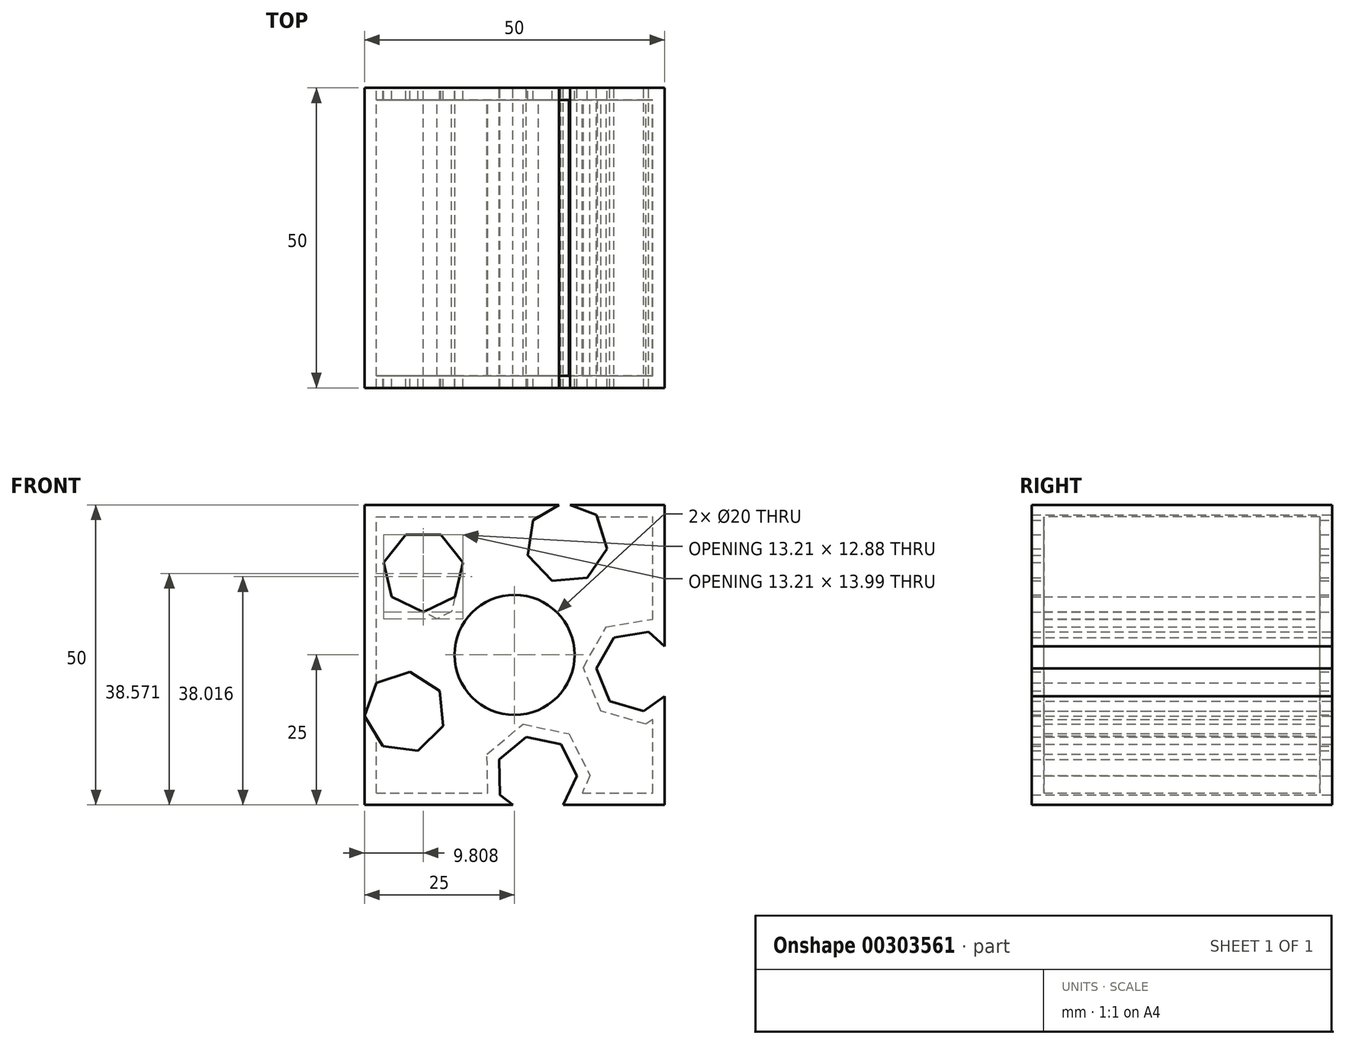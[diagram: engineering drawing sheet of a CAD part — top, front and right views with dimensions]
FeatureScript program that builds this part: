
annotation { "Feature Type Name" : "Feature", "Feature Type Description" : "" }
export const myFeature = defineFeature(function(context is Context, id is Id, definition is map)
    precondition{}
    {
        {
            var Q0;
            Q0=qCreatedBy(makeId("Front.planeOp"),FACE);
            var sketch = newSketch(context, id + "F0", { "sketchPlane" : qUnion([Q0])});
            skLineSegment(sketch, "E0.bottom", {"start": v(0, 0) * mm, "end": v(50, 0) * mm});
            skLineSegment(sketch, "E0.top", {"start": v(0, 50) * mm, "end": v(50, 50) * mm});
            skLineSegment(sketch, "E0.left", {"start": v(0, 0) * mm, "end": v(0, 50) * mm});
            skLineSegment(sketch, "E0.right", {"start": v(50, 0) * mm, "end": v(50, 50) * mm});
            skCircle(sketch, "E1", {"center": v(25, 25) * mm, "radius": 10 * mm});
            skPoint(sketch, "E1.centerSnap0", {"position": v(25, 50) * mm});
            skPoint(sketch, "E1.centerSnap1", {"position": v(50, 25) * mm});
            skLineSegment(sketch, "E2.0", {"start": v(6.87, 45.01) * mm, "end": v(12.75, 45.01) * mm});
            skLineSegment(sketch, "E2.1", {"start": v(12.75, 45.01) * mm, "end": v(16.41, 40.41) * mm});
            skLineSegment(sketch, "E2.2", {"start": v(16.41, 40.41) * mm, "end": v(15.1, 34.68) * mm});
            skLineSegment(sketch, "E2.3", {"start": v(15.1, 34.68) * mm, "end": v(9.8, 32.13) * mm});
            skLineSegment(sketch, "E2.4", {"start": v(9.8, 32.13) * mm, "end": v(4.51, 34.68) * mm});
            skLineSegment(sketch, "E2.5", {"start": v(4.51, 34.68) * mm, "end": v(3.2, 40.41) * mm});
            skLineSegment(sketch, "E2.6", {"start": v(3.2, 40.41) * mm, "end": v(6.87, 45.01) * mm});
            skPoint(sketch, "E2.0.midPoint", {"position": v(9.8, 45.01) * mm});
            skPoint(sketch, "E2.cCircle.center.orphan", {"position": v(9.8, 38.9) * mm});
            skLineSegment(sketch, "E3", {"start": v(0, 50) * mm, "end": v(50, 0) * mm, "construction": true});
            skPoint(sketch, "E4.1.1", {"position": v(48.84, 32.52) * mm});
            skPoint(sketch, "E4.1.2", {"position": v(33.7, 43.67) * mm});
            skPoint(sketch, "E4.1.3", {"position": v(39.52, 45.5) * mm});
            skLineSegment(sketch, "E4.1.4", {"start": v(40.4, 42.7) * mm, "end": v(37.12, 37.82) * mm});
            skLineSegment(sketch, "E4.1.5", {"start": v(38.63, 48.31) * mm, "end": v(40.4, 42.7) * mm});
            skLineSegment(sketch, "E4.1.6", {"start": v(37.12, 37.82) * mm, "end": v(31.26, 37.35) * mm});
            skLineSegment(sketch, "E4.1.7", {"start": v(31.26, 37.35) * mm, "end": v(27.23, 41.63) * mm});
            skLineSegment(sketch, "E4.1.8", {"start": v(27.23, 41.63) * mm, "end": v(28.07, 47.45) * mm});
            skLineSegment(sketch, "E4.1.9", {"start": v(28.07, 47.45) * mm, "end": v(33.15, 50.42) * mm});
            skLineSegment(sketch, "E4.1.10", {"start": v(33.15, 50.42) * mm, "end": v(38.63, 48.31) * mm});
            skPoint(sketch, "E4.2.1", {"position": v(39.34, 4.52) * mm});
            skPoint(sketch, "E4.2.2", {"position": v(45.42, 22.32) * mm});
            skPoint(sketch, "E4.2.3", {"position": v(48.92, 17.32) * mm});
            skLineSegment(sketch, "E4.2.4", {"start": v(46.51, 15.64) * mm, "end": v(40.88, 17.3) * mm});
            skLineSegment(sketch, "E4.2.5", {"start": v(51.33, 19) * mm, "end": v(46.51, 15.64) * mm});
            skLineSegment(sketch, "E4.2.6", {"start": v(40.88, 17.3) * mm, "end": v(38.66, 22.74) * mm});
            skLineSegment(sketch, "E4.2.7", {"start": v(38.66, 22.74) * mm, "end": v(41.54, 27.87) * mm});
            skLineSegment(sketch, "E4.2.8", {"start": v(41.54, 27.87) * mm, "end": v(47.34, 28.82) * mm});
            skLineSegment(sketch, "E4.2.9", {"start": v(47.34, 28.82) * mm, "end": v(51.7, 24.88) * mm});
            skLineSegment(sketch, "E4.2.10", {"start": v(51.7, 24.88) * mm, "end": v(51.33, 19) * mm});
            skPoint(sketch, "E4.3.1", {"position": v(9.78, 5.17) * mm});
            skPoint(sketch, "E4.3.2", {"position": v(28.59, 4.72) * mm});
            skPoint(sketch, "E4.3.3", {"position": v(24.87, -0.12) * mm});
            skLineSegment(sketch, "E4.3.4", {"start": v(22.54, 1.67) * mm, "end": v(22.43, 7.54) * mm});
            skLineSegment(sketch, "E4.3.5", {"start": v(27.2, -1.91) * mm, "end": v(22.54, 1.67) * mm});
            skLineSegment(sketch, "E4.3.6", {"start": v(22.43, 7.54) * mm, "end": v(26.96, 11.3) * mm});
            skLineSegment(sketch, "E4.3.7", {"start": v(26.96, 11.3) * mm, "end": v(32.71, 10.1) * mm});
            skLineSegment(sketch, "E4.3.8", {"start": v(32.71, 10.1) * mm, "end": v(35.36, 4.85) * mm});
            skLineSegment(sketch, "E4.3.9", {"start": v(35.36, 4.85) * mm, "end": v(32.9, -0.5) * mm});
            skLineSegment(sketch, "E4.3.10", {"start": v(32.9, -0.5) * mm, "end": v(27.2, -1.91) * mm});
            skPoint(sketch, "E4.4.1", {"position": v(1.5, 33.55) * mm});
            skPoint(sketch, "E4.4.2", {"position": v(6.74, 15.48) * mm});
            skPoint(sketch, "E4.4.3", {"position": v(1, 17.57) * mm});
            skLineSegment(sketch, "E4.4.4", {"start": v(2, 20.33) * mm, "end": v(7.58, 22.2) * mm});
            skLineSegment(sketch, "E4.4.5", {"start": v(0, 14.8) * mm, "end": v(2, 20.33) * mm});
            skLineSegment(sketch, "E4.4.6", {"start": v(7.58, 22.2) * mm, "end": v(12.52, 19.01) * mm});
            skLineSegment(sketch, "E4.4.7", {"start": v(12.52, 19.01) * mm, "end": v(13.1, 13.16) * mm});
            skLineSegment(sketch, "E4.4.8", {"start": v(13.1, 13.16) * mm, "end": v(8.9, 9.06) * mm});
            skLineSegment(sketch, "E4.4.9", {"start": v(8.9, 9.06) * mm, "end": v(3.06, 9.79) * mm});
            skLineSegment(sketch, "E4.4.10", {"start": v(3.06, 9.79) * mm, "end": v(0, 14.8) * mm});
            skLineSegment(sketch, "E4.anchor1", {"start": v(25, 25) * mm, "end": v(4.51, 34.68) * mm, "construction": true});
            skLineSegment(sketch, "E4.anchor2", {"start": v(25, 25) * mm, "end": v(8.9, 9.06) * mm, "construction": true});
            skSolve(sketch);
        }
        {
            assignVariable(context, id + "F1", {"name" : "extrusion", "anyValue" : 50});
        }
        {
            var Q0;
            Q0=makeQuery(id+"F0.imprint","IMPRINT",FACE,{"disambiguationData":[TD([[makeQuery(id+"F0.imprint","IMPRINT",EDGE,{"derivedFrom":sQuery(id+"F0.wireOp",EDGE,"E2.0")}),1.0]])]});
            extrude(context, id + "F2", {"entities" : qUnion([Q0]), "depth" : (getVariable(context, 'extrusion')) * mm});
        }
        {
            var Q0;
            Q0=makeQuery(id+"F2.opExtrude","SWEPT_FACE",FACE,{"disambiguationData":[OSD([sQuery(id+"F0.wireOp",EDGE,"E1")])]});
            var Q1;
            Q1=makeQuery(id+"F2.opExtrude","SWEPT_FACE",FACE,{"disambiguationData":[OSD([sQuery(id+"F0.wireOp",EDGE,"E4.4.10")])]});
            var Q2;
            Q2=makeQuery(id+"F2.opExtrude","SWEPT_FACE",FACE,{"disambiguationData":[OSD([sQuery(id+"F0.wireOp",EDGE,"E4.4.5")])]});
            var Q3;
            Q3=makeQuery(id+"F2.opExtrude","SWEPT_FACE",FACE,{"disambiguationData":[OSD([sQuery(id+"F0.wireOp",EDGE,"E2.5")])]});
            var Q4;
            Q4=makeQuery(id+"F2.opExtrude","SWEPT_FACE",FACE,{"disambiguationData":[OSD([sQuery(id+"F0.wireOp",EDGE,"E2.4")])]});
            var Q5;
            Q5=makeQuery(id+"F2.opExtrude","SWEPT_FACE",FACE,{"disambiguationData":[OSD([sQuery(id+"F0.wireOp",EDGE,"E2.6")])]});
            var Q6;
            Q6=makeQuery(id+"F2.opExtrude","SWEPT_FACE",FACE,{"disambiguationData":[OSD([sQuery(id+"F0.wireOp",EDGE,"E4.1.8")])]});
            var Q7;
            Q7=makeQuery(id+"F2.opExtrude","SWEPT_FACE",FACE,{"disambiguationData":[OSD([sQuery(id+"F0.wireOp",EDGE,"E4.1.7")])]});
            var Q8;
            Q8=makeQuery(id+"F2.opExtrude","SWEPT_FACE",FACE,{"disambiguationData":[OSD([sQuery(id+"F0.wireOp",EDGE,"E2.0")])]});
            var Q9;
            Q9=makeQuery(id+"F2.opExtrude","SWEPT_FACE",FACE,{"disambiguationData":[OSD([sQuery(id+"F0.wireOp",EDGE,"E2.1")])]});
            var Q10;
            Q10=makeQuery(id+"F2.opExtrude","SWEPT_FACE",FACE,{"disambiguationData":[OSD([sQuery(id+"F0.wireOp",EDGE,"E4.4.4")])]});
            var Q11;
            Q11=makeQuery(id+"F2.opExtrude","SWEPT_FACE",FACE,{"disambiguationData":[OSD([sQuery(id+"F0.wireOp",EDGE,"E4.4.6")])]});
            var Q12;
            Q12=makeQuery(id+"F2.opExtrude","SWEPT_FACE",FACE,{"disambiguationData":[OSD([sQuery(id+"F0.wireOp",EDGE,"E4.1.9")])]});
            var Q13;
            Q13=makeQuery(id+"F2.opExtrude","SWEPT_FACE",FACE,{"disambiguationData":[OSD([sQuery(id+"F0.wireOp",EDGE,"E4.1.10")])]});
            var Q14;
            Q14=makeQuery(id+"F2.opExtrude","SWEPT_FACE",FACE,{"disambiguationData":[OSD([sQuery(id+"F0.wireOp",EDGE,"E4.1.5")])]});
            var Q15;
            Q15=makeQuery(id+"F2.opExtrude","SWEPT_FACE",FACE,{"disambiguationData":[OSD([sQuery(id+"F0.wireOp",EDGE,"E4.1.4")])]});
            var Q16;
            Q16=makeQuery(id+"F2.opExtrude","SWEPT_FACE",FACE,{"disambiguationData":[OSD([sQuery(id+"F0.wireOp",EDGE,"E4.1.6")])]});
            var Q17;
            Q17=makeQuery(id+"F2.opExtrude","SWEPT_FACE",FACE,{"disambiguationData":[OSD([sQuery(id+"F0.wireOp",EDGE,"E4.4.7")])]});
            var Q18;
            Q18=makeQuery(id+"F2.opExtrude","SWEPT_FACE",FACE,{"disambiguationData":[OSD([sQuery(id+"F0.wireOp",EDGE,"E4.4.8")])]});
            var Q19;
            Q19=makeQuery(id+"F2.opExtrude","SWEPT_FACE",FACE,{"disambiguationData":[OSD([sQuery(id+"F0.wireOp",EDGE,"E4.4.9")])]});
            var Q20;
            Q20=makeQuery(id+"F2.opExtrude","SWEPT_FACE",FACE,{"disambiguationData":[OSD([sQuery(id+"F0.wireOp",EDGE,"E2.2")])]});
            shell(context, id + "F3", {"entities" : qUnion([Q0, Q1, Q2, Q3, Q4, Q5, Q6, Q7, Q8, Q9, Q10, Q11, Q12, Q13, Q14, Q15, Q16, Q17, Q18, Q19, Q20]), "thickness" : 2 * mm});
        }
    });
